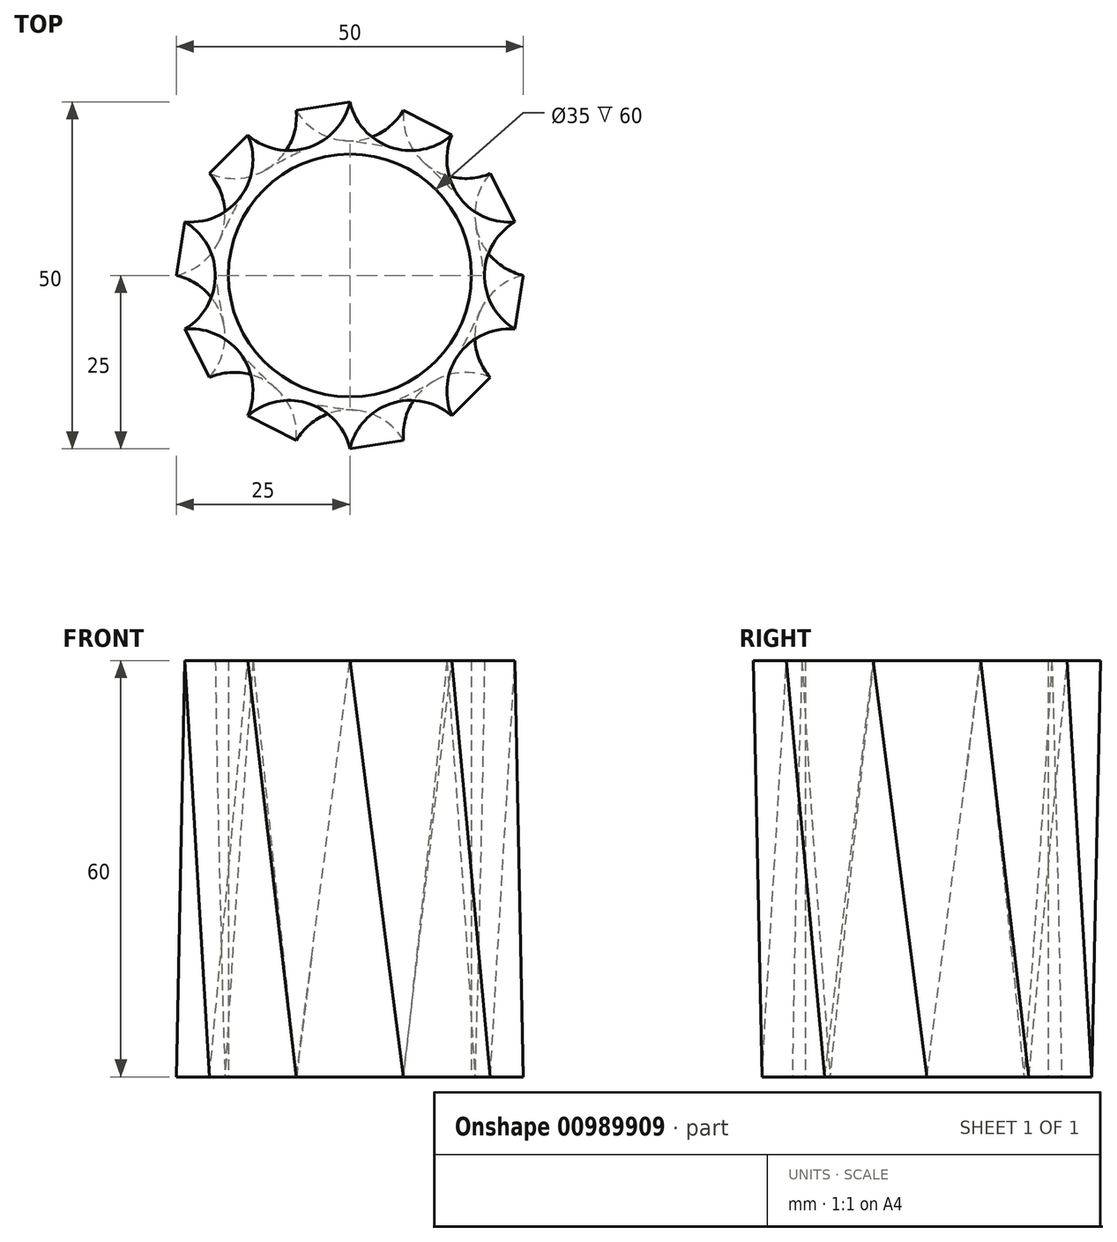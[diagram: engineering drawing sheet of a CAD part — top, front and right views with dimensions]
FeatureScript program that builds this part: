
annotation { "Feature Type Name" : "Feature", "Feature Type Description" : "" }
export const myFeature = defineFeature(function(context is Context, id is Id, definition is map)
    precondition{}
    {
        {
            var Q0;
            Q0=qCreatedBy(makeId("Top.planeOp"),FACE);
            var sketch = newSketch(context, id + "F0", { "sketchPlane" : qUnion([Q0])});
            skCircle(sketch, "E0.cCircle", {"center": v(0, 0) * mm, "radius": 25 * mm, "construction": true});
            skLineSegment(sketch, "E0.0", {"start": v(-25, 0) * mm, "end": v(-20.23, 14.7) * mm});
            skLineSegment(sketch, "E0.1", {"start": v(-20.23, 14.7) * mm, "end": v(-7.73, 23.78) * mm});
            skLineSegment(sketch, "E0.2", {"start": v(-7.73, 23.78) * mm, "end": v(7.73, 23.78) * mm});
            skLineSegment(sketch, "E0.3", {"start": v(7.73, 23.78) * mm, "end": v(20.23, 14.7) * mm});
            skLineSegment(sketch, "E0.4", {"start": v(20.23, 14.7) * mm, "end": v(25, 0) * mm});
            skLineSegment(sketch, "E0.5", {"start": v(25, 0) * mm, "end": v(20.23, -14.7) * mm});
            skLineSegment(sketch, "E0.6", {"start": v(20.23, -14.7) * mm, "end": v(7.73, -23.78) * mm});
            skLineSegment(sketch, "E0.7", {"start": v(7.73, -23.78) * mm, "end": v(-7.73, -23.78) * mm});
            skLineSegment(sketch, "E0.8", {"start": v(-7.73, -23.78) * mm, "end": v(-20.23, -14.7) * mm});
            skLineSegment(sketch, "E0.9", {"start": v(-20.23, -14.7) * mm, "end": v(-25, 0) * mm});
            skLineSegment(sketch, "E1", {"start": v(-20.23, 14.7) * mm, "end": v(20.23, -14.7) * mm, "construction": true});
            skLineSegment(sketch, "E2", {"start": v(-7.73, 23.78) * mm, "end": v(7.73, -23.78) * mm, "construction": true});
            skLineSegment(sketch, "E3", {"start": v(7.73, 23.78) * mm, "end": v(-7.73, -23.78) * mm, "construction": true});
            skLineSegment(sketch, "E4", {"start": v(20.23, 14.7) * mm, "end": v(-20.23, -14.7) * mm, "construction": true});
            skLineSegment(sketch, "E5", {"start": v(-25, 0) * mm, "end": v(25, 0) * mm, "construction": true});
            skArc(sketch, "E6", {"start": v(-7.73, 23.78) * mm, "mid": v(0, 19.4) * mm, "end": v(7.73, 23.78) * mm});
            skArc(sketch, "E7", {"start": v(7.73, 23.78) * mm, "mid": v(11.4, 15.69) * mm, "end": v(20.23, 14.7) * mm});
            skArc(sketch, "E8", {"start": v(20.23, 14.7) * mm, "mid": v(18.44, 6) * mm, "end": v(25, 0) * mm});
            skArc(sketch, "E9", {"start": v(25, 0) * mm, "mid": v(18.44, -6) * mm, "end": v(20.23, -14.7) * mm});
            skArc(sketch, "E10", {"start": v(20.23, -14.7) * mm, "mid": v(11.4, -15.69) * mm, "end": v(7.73, -23.78) * mm});
            skArc(sketch, "E11", {"start": v(7.73, -23.78) * mm, "mid": v(0, -19.4) * mm, "end": v(-7.73, -23.78) * mm});
            skArc(sketch, "E12", {"start": v(-7.73, -23.78) * mm, "mid": v(-11.4, -15.69) * mm, "end": v(-20.23, -14.7) * mm});
            skArc(sketch, "E13", {"start": v(-20.23, -14.7) * mm, "mid": v(-18.44, -6) * mm, "end": v(-25, 0) * mm});
            skArc(sketch, "E14", {"start": v(-25, 0) * mm, "mid": v(-18.44, 6) * mm, "end": v(-20.23, 14.7) * mm});
            skArc(sketch, "E15", {"start": v(-20.23, 14.7) * mm, "mid": v(-11.4, 15.69) * mm, "end": v(-7.73, 23.78) * mm});
            skSolve(sketch);
        }
        {
            var Q0;
            Q0=qCreatedBy(makeId("Top.planeOp"),FACE);
            cPlane(context, id + "F1", {"entities" : qUnion([Q0]), "cplaneType" : CPlaneType.OFFSET, "offset" : 60 * mm, "width" : 150 * mm, "height" : 150 * mm});
        }
        {
            var Q0;
            Q0=qCreatedBy(id+"F1.planeOp",FACE);
            var sketch = newSketch(context, id + "F2", { "sketchPlane" : qUnion([Q0])});
            skCircle(sketch, "E16.cCircle", {"center": v(0, 0) * mm, "radius": 25 * mm, "construction": true});
            skLineSegment(sketch, "E16.0", {"start": v(0, 25) * mm, "end": v(14.7, 20.23) * mm});
            skLineSegment(sketch, "E16.1", {"start": v(14.7, 20.23) * mm, "end": v(23.78, 7.73) * mm});
            skLineSegment(sketch, "E16.2", {"start": v(23.78, 7.73) * mm, "end": v(23.78, -7.73) * mm});
            skLineSegment(sketch, "E16.3", {"start": v(23.78, -7.73) * mm, "end": v(14.7, -20.23) * mm});
            skLineSegment(sketch, "E16.4", {"start": v(14.7, -20.23) * mm, "end": v(0, -25) * mm});
            skLineSegment(sketch, "E16.5", {"start": v(0, -25) * mm, "end": v(-14.7, -20.23) * mm});
            skLineSegment(sketch, "E16.6", {"start": v(-14.7, -20.23) * mm, "end": v(-23.78, -7.73) * mm});
            skLineSegment(sketch, "E16.7", {"start": v(-23.78, -7.73) * mm, "end": v(-23.78, 7.73) * mm});
            skLineSegment(sketch, "E16.8", {"start": v(-23.78, 7.73) * mm, "end": v(-14.7, 20.23) * mm});
            skLineSegment(sketch, "E16.9", {"start": v(-14.7, 20.23) * mm, "end": v(0, 25) * mm});
            skLineSegment(sketch, "E17", {"start": v(0, 25) * mm, "end": v(0, -25) * mm, "construction": true});
            skLineSegment(sketch, "E18", {"start": v(-14.7, -20.23) * mm, "end": v(14.7, 20.23) * mm, "construction": true});
            skLineSegment(sketch, "E19", {"start": v(-14.7, 20.23) * mm, "end": v(14.7, -20.23) * mm, "construction": true});
            skLineSegment(sketch, "E20", {"start": v(-23.78, -7.73) * mm, "end": v(23.78, 7.73) * mm, "construction": true});
            skLineSegment(sketch, "E21", {"start": v(23.78, -7.73) * mm, "end": v(-23.78, 7.73) * mm, "construction": true});
            skArc(sketch, "E22", {"start": v(-14.7, 20.23) * mm, "mid": v(-6, 18.44) * mm, "end": v(0, 25) * mm});
            skArc(sketch, "E23", {"start": v(0, 25) * mm, "mid": v(6, 18.44) * mm, "end": v(14.7, 20.23) * mm});
            skArc(sketch, "E24", {"start": v(14.7, 20.23) * mm, "mid": v(15.69, 11.4) * mm, "end": v(23.78, 7.73) * mm});
            skArc(sketch, "E25", {"start": v(23.78, 7.73) * mm, "mid": v(19.4, 0) * mm, "end": v(23.78, -7.73) * mm});
            skArc(sketch, "E26", {"start": v(23.78, -7.73) * mm, "mid": v(15.69, -11.4) * mm, "end": v(14.7, -20.23) * mm});
            skArc(sketch, "E27", {"start": v(14.7, -20.23) * mm, "mid": v(6, -18.44) * mm, "end": v(0, -25) * mm});
            skArc(sketch, "E28", {"start": v(0, -25) * mm, "mid": v(-6, -18.44) * mm, "end": v(-14.7, -20.23) * mm});
            skArc(sketch, "E29", {"start": v(-14.7, -20.23) * mm, "mid": v(-15.69, -11.4) * mm, "end": v(-23.78, -7.73) * mm});
            skArc(sketch, "E30", {"start": v(-23.78, -7.73) * mm, "mid": v(-19.4, 0) * mm, "end": v(-23.78, 7.73) * mm});
            skArc(sketch, "E31", {"start": v(-23.78, 7.73) * mm, "mid": v(-15.69, 11.4) * mm, "end": v(-14.7, 20.23) * mm});
            skSolve(sketch);
        }
        {
            var Q0;
            Q0=makeQuery(id+"F0.imprint","IMPRINT",FACE,{"disambiguationData":[TD([[makeQuery(id+"F0.imprint","IMPRINT",EDGE,{"derivedFrom":sQuery(id+"F0.wireOp",EDGE,"E6")}),-1.0]])]});
            var Q1;
            Q1=makeQuery(id+"F2.imprint","IMPRINT",FACE,{"disambiguationData":[TD([[makeQuery(id+"F2.imprint","IMPRINT",EDGE,{"derivedFrom":sQuery(id+"F2.wireOp",EDGE,"E22")}),-1.0]])]});
            loft(context, id + "F3", {"sheetProfilesArray" : [{ "sheetProfileEntities" : qUnion([Q0]) }, { "sheetProfileEntities" : qUnion([Q1]) }]});
        }
        {
            var Q0;
            Q0=makeQuery(id+"F0.imprint","IMPRINT",FACE,{"disambiguationData":[TD([[makeQuery(id+"F0.imprint","IMPRINT",EDGE,{"derivedFrom":sQuery(id+"F0.wireOp",EDGE,"E6")}),-1.0]])]});
            var sketch = newSketch(context, id + "F4", { "sketchPlane" : qUnion([Q0])});
            skCircle(sketch, "E32", {"center": v(0, 0) * mm, "radius": 17.5 * mm});
            skSolve(sketch);
        }
        {
            var Q0;
            Q0=makeQuery(id+"F4.imprint","IMPRINT",FACE,{"disambiguationData":[TD([[makeQuery(id+"F4.imprint","IMPRINT",EDGE,{"derivedFrom":sQuery(id+"F4.wireOp",EDGE,"E32")}),1.0]])]});
            extrude(context, id + "F5", {"entities" : qUnion([Q0]), "operationType" : NewBodyOperationType.REMOVE, "endBound" : BoundingType.THROUGH_ALL, "depth" : 25 * mm, "offsetDistance" : 25 * mm});
        }
    });
